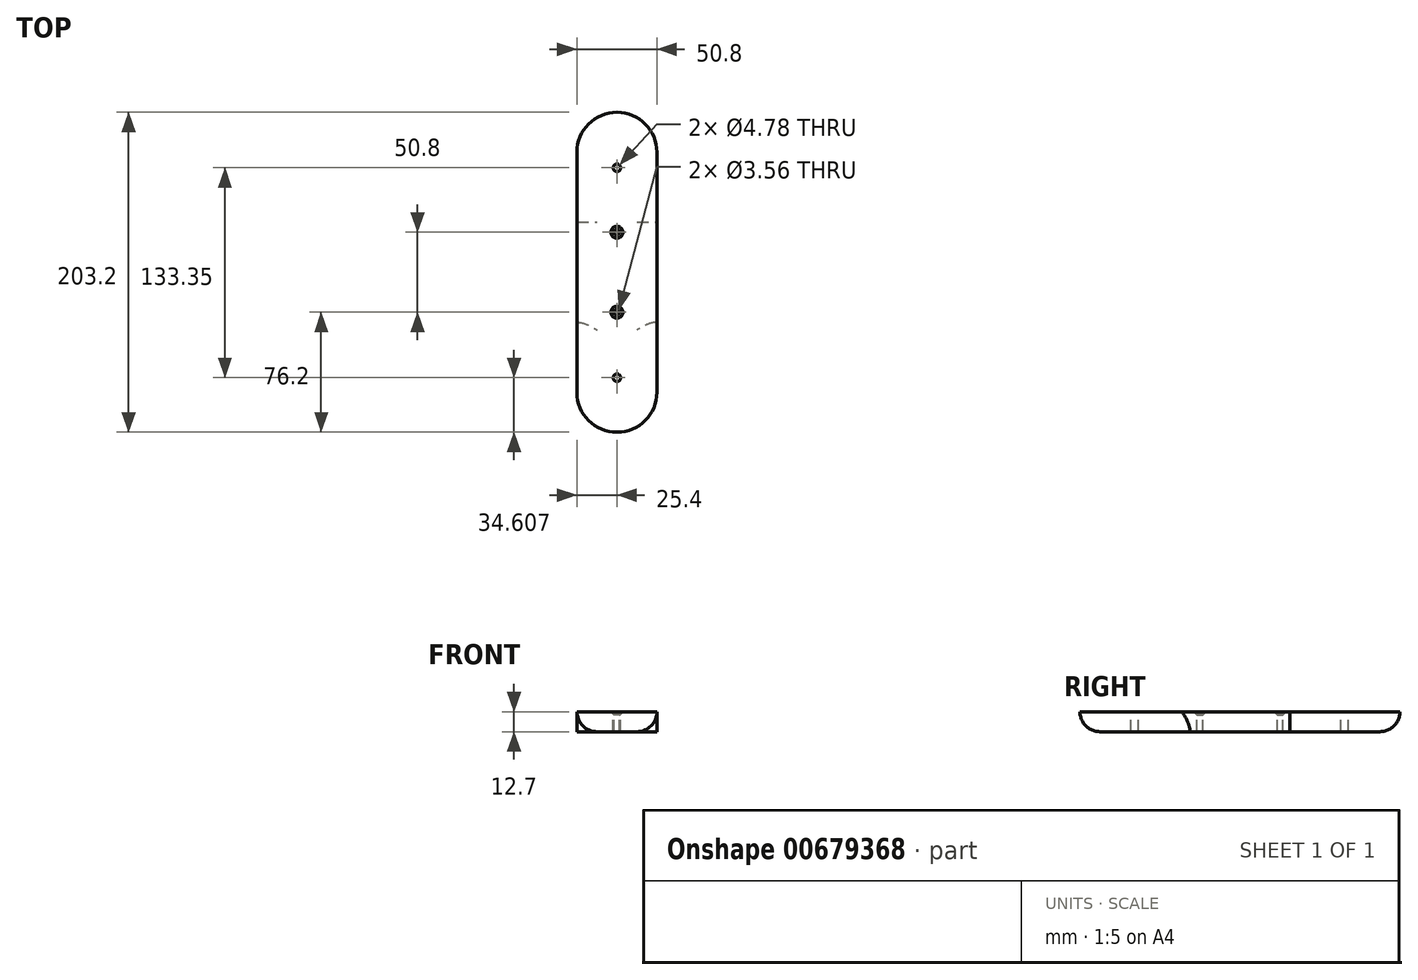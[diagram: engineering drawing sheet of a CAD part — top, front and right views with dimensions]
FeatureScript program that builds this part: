
annotation { "Feature Type Name" : "Feature", "Feature Type Description" : "" }
export const myFeature = defineFeature(function(context is Context, id is Id, definition is map)
    precondition{}
    {
        {
            var Q0;
            Q0=qCreatedBy(makeId("Top.planeOp"),FACE);
            var sketch = newSketch(context, id + "F0", { "sketchPlane" : qUnion([Q0])});
            skLineSegment(sketch, "E0.left", {"start": v(25.4, 76.2) * mm, "end": v(25.4, -76.2) * mm});
            skLineSegment(sketch, "E0.right", {"start": v(-25.4, 76.2) * mm, "end": v(-25.4, -76.2) * mm});
            skPoint(sketch, "E0.middle", {"position": v(0, 0) * mm});
            skArc(sketch, "E1", {"start": v(-25.4, 76.2) * mm, "mid": v(0, 101.6) * mm, "end": v(25.4, 76.2) * mm});
            skArc(sketch, "E2", {"start": v(25.4, -76.2) * mm, "mid": v(0, -101.6) * mm, "end": v(-25.4, -76.2) * mm});
            skPoint(sketch, "E3", {"position": v(0, 66.36) * mm});
            skPoint(sketch, "E4", {"position": v(0, 25.4) * mm});
            skPoint(sketch, "E5", {"position": v(0, -25.4) * mm});
            skPoint(sketch, "E6", {"position": v(0, -67) * mm});
            skSolve(sketch);
        }
        {
            var Q0;
            Q0 = qSketchRegion(id + "F0", true);
            extrude(context, id + "F1", {"entities" : qUnion([Q0]), "oppositeDirection" : true, "depth" : 12.7 * mm, "offsetDistance" : 25.4 * mm});
        }
        {
            var Q0;
            Q0=sQuery(id+"F0.wireOp",VERTEX,"E3");
            var Q1;
            Q1=sQuery(id+"F0.wireOp",VERTEX,"E6");
            var Q2;
            Q2=makeQuery(id+"F1.opExtrude","SWEPT_BODY",BODY,{"disambiguationData":[OSD([sQuery(id+"F0.wireOp",EDGE,"E0.left"),sQuery(id+"F0.wireOp",EDGE,"E0.right"),sQuery(id+"F0.wireOp",EDGE,"E1"),sQuery(id+"F0.wireOp",EDGE,"E2")])]});
            hole(context, id + "F2", {"style" : HoleStyle.SIMPLE, "endStyle" : HoleEndStyle.THROUGH, "holeDiameter" : 4.78 * mm, "majorDiameter" : 6.35 * mm, "isTappedThrough" : true, "tappedDepth" : 12.7 * mm, "tapClearance" : 3, "locations" : qUnion([Q0, Q1]), "scope" : qUnion([Q2])});
        }
        {
            var Q0;
            Q0=sQuery(id+"F0.wireOp",VERTEX,"E4");
            var Q1;
            Q1=sQuery(id+"F0.wireOp",VERTEX,"E5");
            var Q2;
            Q2=makeQuery(id+"F1.opExtrude","SWEPT_BODY",BODY,{"disambiguationData":[OSD([sQuery(id+"F0.wireOp",EDGE,"E0.left"),sQuery(id+"F0.wireOp",EDGE,"E0.right"),sQuery(id+"F0.wireOp",EDGE,"E1"),sQuery(id+"F0.wireOp",EDGE,"E2")])]});
            hole(context, id + "F3", {"style" : HoleStyle.C_SINK, "endStyle" : HoleEndStyle.THROUGH, "holeDiameter" : 3.56 * mm, "cSinkDiameter" : 7.62 * mm, "cSinkAngle" : 90 * degree, "majorDiameter" : 6.35 * mm, "isTappedThrough" : true, "tappedDepth" : 12.7 * mm, "tapClearance" : 3, "locations" : qUnion([Q0, Q1]), "scope" : qUnion([Q2])});
        }
        {
            var Q0;
            Q0=makeQuery(id+"F1.opExtrude","CAP_EDGE",EDGE,{"disambiguationData":[OSD([sQuery(id+"F0.wireOp",EDGE,"E2")])],"isStart":false});
            var Q1;
            Q1=makeQuery(id+"F1.opExtrude","CAP_EDGE",EDGE,{"disambiguationData":[OSD([sQuery(id+"F0.wireOp",EDGE,"E0.right")])],"isStart":false});
            var Q2;
            Q2=makeQuery(id+"F1.opExtrude","CAP_EDGE",EDGE,{"disambiguationData":[OSD([sQuery(id+"F0.wireOp",EDGE,"E1")])],"isStart":false});
            var Q3;
            Q3=makeQuery(id+"F1.opExtrude","CAP_EDGE",EDGE,{"disambiguationData":[OSD([sQuery(id+"F0.wireOp",EDGE,"E0.left")])],"isStart":false});
            fillet(context, id + "F4", {"entities" : qUnion([Q0, Q1, Q2, Q3]), "radius" : 12.7 * mm, "allowEdgeOverflow" : false});
        }
        {
            var Q0;
            Q0=qCreatedBy(makeId("Front.planeOp"),FACE);
            var sketch = newSketch(context, id + "F5", { "sketchPlane" : qUnion([Q0])});
            skLineSegment(sketch, "E7.top", {"start": v(-25.4, -12.7) * mm, "end": v(-12.7, -12.7) * mm});
            skLineSegment(sketch, "E7.left", {"start": v(-25.4, 0) * mm, "end": v(-25.4, -12.7) * mm});
            skLineSegment(sketch, "E7.right", {"start": v(25.4, 0) * mm, "end": v(25.4, -12.7) * mm});
            skArc(sketch, "E8.0", {"start": v(-12.7, -12.7) * mm, "mid": v(-21.68, -8.98) * mm, "end": v(-25.4, 0) * mm});
            skArc(sketch, "E8.1", {"start": v(25.4, 0) * mm, "mid": v(21.68, -8.98) * mm, "end": v(12.7, -12.7) * mm});
            skLineSegment(sketch, "E9.trimOffspring", {"start": v(12.7, -12.7) * mm, "end": v(25.4, -12.7) * mm});
            skSolve(sketch);
        }
        {
            var Q0;
            Q0 = qSketchRegion(id + "F5", true);
            extrude(context, id + "F6", {"entities" : qUnion([Q0]), "operationType" : NewBodyOperationType.ADD, "depth" : 31.75 * mm, "offsetDistance" : 25.4 * mm, "hasSecondDirection" : true, "secondDirectionOppositeDirection" : true, "secondDirectionDepth" : 31.75 * mm});
        }
        {
            var Q0;
            Q0=makeQuery(id+"F6.opExtrude","CAP_EDGE",EDGE,{"disambiguationData":[OSD([sQuery(id+"F5.wireOp",EDGE,"E8.1")])],"isStart":false});
            var Q1;
            Q1=makeQuery(id+"F6.opExtrude","CAP_EDGE",EDGE,{"disambiguationData":[OSD([sQuery(id+"F5.wireOp",EDGE,"E8.0")])],"isStart":false});
            var Q2;
            Q2=makeQuery(id+"F6.opExtrude","CAP_EDGE",EDGE,{"disambiguationData":[OSD([sQuery(id+"F5.wireOp",EDGE,"E8.0")])],"isStart":true});
            var Q3;
            Q3=makeQuery(id+"F6.opExtrude","CAP_EDGE",EDGE,{"disambiguationData":[OSD([sQuery(id+"F5.wireOp",EDGE,"E8.1")])],"isStart":true});
            fillet(context, id + "F7", {"entities" : qUnion([Q0, Q1, Q2, Q3]), "radius" : 5.08 * mm, "tangentPropagation" : true, "allowEdgeOverflow" : false});
        }
    });
